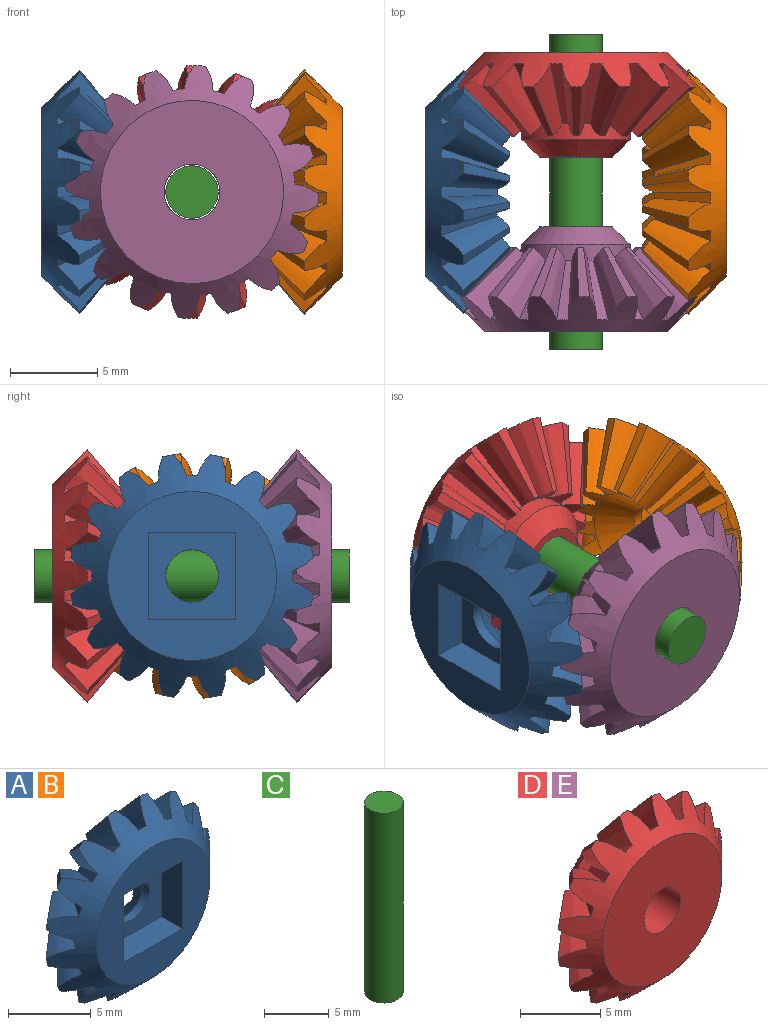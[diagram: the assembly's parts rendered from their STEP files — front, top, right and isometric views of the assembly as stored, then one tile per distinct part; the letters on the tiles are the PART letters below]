
ASSEMBLY  parts=5 mates=2
PART A: 74 faces, bbox 14.1x4.8x14.1 mm
  f0: bspline ~3.9x3.32mm, area 6.1mm2, adj f1,f16,f66,f71
  f1: cone r=6.97mm half-angle=45.1deg, axis (0,1,0), area 76.4mm2, adj f0,f2,f3,f4,f5,f6,f7,f8
  f2: bspline ~3.9x3.81mm, area 6.1mm2, adj f1,f24,f64,f66
  f3: bspline ~3.9x3.32mm, area 6.1mm2, adj f1,f58,f66,f73
  f4: bspline ~3.91x3.19mm, area 6.1mm2, adj f1,f59,f62,f66
  f5: bspline ~3.91x3.19mm, area 6.1mm2, adj f1,f19,f66,f73
  f6: plane 3.2x2.55mm, normal (0.72,0.62,-0.3), area 2mm2, adj f1,f12,f66,f69
  f7: cone r=3.9mm half-angle=50deg, axis (0,-1,0), area 2mm2, adj f1,f29,f37,f66
  f8: cone r=3.9mm half-angle=50deg, axis (0,-1,0), area 2mm2, adj f1,f28,f61,f66
  f9: bspline ~3.9x3.18mm, area 6.1mm2, adj f1,f32,f66,f72
  f10: bspline ~3.91x3.82mm, area 6.1mm2, adj f1,f15,f64,f66
  f11: bspline ~3.91x3.82mm, area 6.1mm2, adj f1,f33,f40,f66
  f12: bspline ~3.91x3.19mm, area 6.1mm2, adj f1,f6,f36,f66
  f13: bspline ~3.9x3.81mm, area 6.1mm2, adj f1,f23,f33,f66
  f14: bspline ~3.91x3.33mm, area 6.1mm2, adj f1,f66,f71,f72
  f15: cone r=3.9mm half-angle=50deg, axis (0,-1,0), area 2mm2, adj f1,f10,f26,f66
  f16: cone r=3.9mm half-angle=50deg, axis (0,-1,0), area 2mm2, adj f0,f1,f22,f66
  f17: plane 9.67x9.67mm, normal (0,-1,0), area 48.4mm2, adj f1,f45,f46,f48,f49
  f18: cylinder r=1.5mm len=3mm, axis (0,1,0), area 5.7mm2, adj f47,f50
  f19: plane 3.2x2.55mm, normal (-0.3,0.62,-0.72), area 2mm2, adj f1,f5,f60,f66
  f20: plane 3.2x2.16mm, normal (0.55,0.62,-0.55), area 2mm2, adj f1,f34,f51,f66
  f21: bspline ~3.91x3.87mm, area 6.1mm2, adj f1,f24,f30,f66
  f22: bspline ~3.91x3.19mm, area 6.1mm2, adj f1,f16,f39,f66
  f23: cone r=3.9mm half-angle=50deg, axis (0,-1,0), area 2mm2, adj f1,f13,f66,f70
  f24: cone r=3.9mm half-angle=50deg, axis (0,-1,0), area 2mm2, adj f1,f2,f21,f66
  f25: bspline ~3.91x3.33mm, area 6.1mm2, adj f1,f55,f65,f66
  f26: bspline ~3.92x3.89mm, area 6.1mm2, adj f1,f15,f39,f66
  f27: plane 3.2x2.55mm, normal (-0.72,0.62,-0.3), area 2mm2, adj f1,f37,f63,f66
  f28: bspline ~3.92x3.89mm, area 6.1mm2, adj f1,f8,f59,f66
  f29: bspline ~3.9x3.81mm, area 6.1mm2, adj f1,f7,f44,f66
  f30: plane 3.2x2.55mm, normal (-0.3,0.62,0.72), area 2mm2, adj f1,f21,f42,f66
  f31: cone r=3.9mm half-angle=50deg, axis (0,-1,0), area 2mm2, adj f1,f34,f35,f66
  f32: plane 3.2x2.55mm, normal (0.72,0.62,0.3), area 2mm2, adj f1,f9,f66,f70
  f33: plane 3.2x2.56mm, normal (0.78,0.62,0), area 2mm2, adj f1,f11,f13,f66
  f34: bspline ~3.91x3.33mm, area 6.1mm2, adj f1,f20,f31,f66
  f35: bspline ~3.9x3.18mm, area 6.1mm2, adj f1,f31,f52,f66
  f36: cone r=3.9mm half-angle=50deg, axis (0,-1,0), area 2mm2, adj f1,f12,f51,f66
  f37: bspline ~3.91x3.87mm, area 6.1mm2, adj f1,f7,f27,f66
  f38: bspline ~3.91x3.82mm, area 6.1mm2, adj f1,f43,f54,f66
  f39: plane 3.2x2.55mm, normal (0.3,0.62,0.72), area 2mm2, adj f1,f22,f26,f66
  f40: cone r=3.9mm half-angle=50deg, axis (0,-1,0), area 2mm2, adj f1,f11,f66,f69
  f41: bspline ~3.9x3.32mm, area 6.1mm2, adj f1,f55,f62,f66
  f42: bspline ~3.9x3.18mm, area 6.1mm2, adj f1,f30,f65,f66
  f43: plane 3.2x2.56mm, normal (0,0.62,-0.78), area 2mm2, adj f1,f38,f66,f67
  f44: plane 3.2x2.56mm, normal (-0.78,0.62,0), area 2mm2, adj f1,f29,f61,f66
  f45: plane 5x1.8mm, normal (0,0,-1), area 9mm2, adj f17,f46,f47,f49
  f46: plane 5x1.8mm, normal (1,0,0), area 9mm2, adj f17,f45,f47,f48
  f47: plane 5x5mm, normal (0,-1,0), area 17.9mm2, adj f18,f45,f46,f48,f49
  f48: plane 5x1.8mm, normal (0,0,1), area 9mm2, adj f17,f46,f47,f49
  f49: plane 5x1.8mm, normal (-1,0,0), area 9mm2, adj f17,f45,f47,f48
  f50: cone r=1.5mm half-angle=45deg, axis (0,1,0), area 32.7mm2, adj f18,f66
  f51: bspline ~3.9x3.32mm, area 6.1mm2, adj f1,f20,f36,f66
  f52: plane 3.2x2.55mm, normal (0.3,0.62,-0.72), area 2mm2, adj f1,f35,f53,f66
  f53: bspline ~3.91x3.87mm, area 6.1mm2, adj f1,f52,f66,f68
  f54: cone r=3.9mm half-angle=50deg, axis (0,-1,0), area 2mm2, adj f1,f38,f60,f66
  f55: plane 3.2x2.16mm, normal (-0.55,0.62,0.55), area 2mm2, adj f1,f25,f41,f66
  f56: cone r=3.9mm half-angle=50deg, axis (0,-1,0), area 2mm2, adj f1,f57,f63,f66
  f57: bspline ~3.91x3.33mm, area 6.1mm2, adj f1,f56,f58,f66
  f58: plane 3.2x2.16mm, normal (-0.55,0.62,-0.55), area 2mm2, adj f1,f3,f57,f66
  f59: plane 3.2x2.55mm, normal (-0.72,0.62,0.3), area 2mm2, adj f1,f4,f28,f66
  f60: bspline ~3.92x3.89mm, area 6.1mm2, adj f1,f19,f54,f66
  f61: bspline ~3.91x3.82mm, area 6.1mm2, adj f1,f8,f44,f66
  f62: cone r=3.9mm half-angle=50deg, axis (0,-1,0), area 2mm2, adj f1,f4,f41,f66
  f63: bspline ~3.9x3.18mm, area 6.1mm2, adj f1,f27,f56,f66
  f64: plane 3.2x2.56mm, normal (0,0.62,0.78), area 2mm2, adj f1,f2,f10,f66
  f65: cone r=3.9mm half-angle=50deg, axis (0,-1,0), area 2mm2, adj f1,f25,f42,f66
  f66: cone r=3.9mm half-angle=45.1deg, axis (0,1,0), area 13mm2, adj f0,f2,f3,f4,f5,f6,f7,f8
  f67: bspline ~3.9x3.81mm, area 6.1mm2, adj f1,f43,f66,f68
  f68: cone r=3.9mm half-angle=50deg, axis (0,-1,0), area 2mm2, adj f1,f53,f66,f67
  f69: bspline ~3.92x3.89mm, area 6.1mm2, adj f1,f6,f40,f66
  f70: bspline ~3.91x3.87mm, area 6.1mm2, adj f1,f23,f32,f66
  f71: plane 3.2x2.16mm, normal (0.55,0.62,0.55), area 2mm2, adj f0,f1,f14,f66
  f72: cone r=3.9mm half-angle=50deg, axis (0,-1,0), area 2mm2, adj f1,f9,f14,f66
  f73: cone r=3.9mm half-angle=50deg, axis (0,-1,0), area 2mm2, adj f1,f3,f5,f66
PART B: same geometry as A
PART C: 3 faces, bbox 3x3x18 mm
  f0: plane 3x3mm, normal (0,0,-1), area 7.1mm2, adj f2
  f1: plane 3x3mm, normal (0,0,1), area 7.1mm2, adj f2
  f2: cylinder r=1.5mm len=18mm, axis (0,0,-1), area 169.6mm2, adj f0,f1
PART D: 71 faces, bbox 14.5x6x14.5 mm
  f0: bspline ~4.12x4.03mm, area 6.6mm2, adj f2,f7,f27,f46
  f1: bspline ~4.13x4.09mm, area 6.6mm2, adj f2,f27,f46,f51
  f2: cone r=3.9mm half-angle=45.1deg, axis (0,1,0), area 13mm2, adj f0,f1,f3,f4,f5,f6,f7,f8
  f3: bspline ~4.12x3.5mm, area 6.6mm2, adj f2,f4,f28,f46
  f4: plane 3.43x2.29mm, normal (-0.55,0.62,-0.55), area 2.2mm2, adj f2,f3,f29,f46
  f5: bspline ~4.13x3.38mm, area 6.6mm2, adj f2,f46,f62,f70
  f6: plane 3.43x2.29mm, normal (-0.55,0.62,0.55), area 2.2mm2, adj f2,f46,f61,f63
  f7: plane 3.42x2.73mm, normal (0,0.62,-0.78), area 2.2mm2, adj f0,f2,f8,f46
  f8: bspline ~4.12x4.03mm, area 6.6mm2, adj f2,f7,f37,f46
  f9: bspline ~4.12x4.03mm, area 6.6mm2, adj f2,f33,f46,f67
  f10: bspline ~4.13x4.09mm, area 6.6mm2, adj f2,f33,f36,f46
  f11: bspline ~4.13x3.38mm, area 6.6mm2, adj f2,f12,f46,f65
  f12: plane 3.43x2.72mm, normal (-0.3,0.62,0.72), area 2.2mm2, adj f2,f11,f46,f69
  f13: bspline ~4.13x3.38mm, area 6.6mm2, adj f2,f14,f38,f46
  f14: plane 3.43x2.72mm, normal (0.3,0.62,-0.72), area 2.2mm2, adj f2,f13,f45,f46
  f15: cone r=3.9mm half-angle=50deg, axis (0,-1,0), area 2.2mm2, adj f2,f21,f39,f46
  f16: bspline ~4.12x4.03mm, area 6.6mm2, adj f2,f46,f59,f60
  f17: bspline ~4.13x4.09mm, area 6.6mm2, adj f2,f46,f59,f70
  f18: plane 3.43x2.72mm, normal (-0.72,0.62,-0.3), area 2.2mm2, adj f2,f46,f48,f50
  f19: plane 3.42x2.73mm, normal (0,0.62,0.78), area 2.2mm2, adj f2,f20,f46,f64
  f20: bspline ~4.12x4.03mm, area 6.6mm2, adj f2,f19,f32,f46
  f21: bspline ~4.13x4.09mm, area 6.6mm2, adj f2,f15,f35,f46
  f22: bspline ~4.13x3.38mm, area 6.6mm2, adj f2,f36,f42,f46
  f23: bspline ~4.13x3.51mm, area 6.6mm2, adj f2,f38,f41,f46
  f24: bspline ~4.13x3.51mm, area 6.6mm2, adj f2,f40,f46,f68
  f25: bspline ~4.12x3.5mm, area 6.6mm2, adj f2,f40,f44,f46
  f26: bspline ~4.13x3.38mm, area 6.6mm2, adj f2,f31,f44,f46
  f27: cone r=3.9mm half-angle=50deg, axis (0,-1,0), area 2.2mm2, adj f0,f1,f2,f46
  f28: cone r=3.9mm half-angle=50deg, axis (0,-1,0), area 2.2mm2, adj f2,f3,f46,f52
  f29: bspline ~4.13x3.51mm, area 6.6mm2, adj f2,f4,f46,f49
  f30: bspline ~4.13x4.09mm, area 6.6mm2, adj f2,f31,f32,f46
  f31: plane 3.43x2.72mm, normal (0.3,0.62,0.72), area 2.2mm2, adj f2,f26,f30,f46
  f32: cone r=3.9mm half-angle=50deg, axis (0,-1,0), area 2.2mm2, adj f2,f20,f30,f46
  f33: cone r=3.9mm half-angle=50deg, axis (0,-1,0), area 2.2mm2, adj f2,f9,f10,f46
  f34: bspline ~4.12x3.5mm, area 6.6mm2, adj f2,f41,f42,f46
  f35: plane 3.43x2.72mm, normal (0.72,0.62,0.3), area 2.2mm2, adj f2,f21,f43,f46
  f36: plane 3.43x2.72mm, normal (0.72,0.62,-0.3), area 2.2mm2, adj f2,f10,f22,f46
  f37: cone r=3.9mm half-angle=50deg, axis (0,-1,0), area 2.2mm2, adj f2,f8,f45,f46
  f38: cone r=3.9mm half-angle=50deg, axis (0,-1,0), area 2.2mm2, adj f2,f13,f23,f46
  f39: bspline ~4.12x4.03mm, area 6.6mm2, adj f2,f15,f46,f67
  f40: plane 3.43x2.29mm, normal (0.55,0.62,0.55), area 2.2mm2, adj f2,f24,f25,f46
  f41: plane 3.43x2.29mm, normal (0.55,0.62,-0.55), area 2.2mm2, adj f2,f23,f34,f46
  f42: cone r=3.9mm half-angle=50deg, axis (0,-1,0), area 2.2mm2, adj f2,f22,f34,f46
  f43: bspline ~4.13x3.38mm, area 6.6mm2, adj f2,f35,f46,f68
  f44: cone r=3.9mm half-angle=50deg, axis (0,-1,0), area 2.2mm2, adj f2,f25,f26,f46
  f45: bspline ~4.13x4.09mm, area 6.6mm2, adj f2,f14,f37,f46
  f46: cone r=6.97mm half-angle=45.1deg, axis (0,1,0), area 69.8mm2, adj f0,f1,f3,f4,f5,f6,f7,f8
  f47: bspline ~4.12x4.03mm, area 6.6mm2, adj f2,f46,f53,f60
  f48: bspline ~4.13x3.38mm, area 6.6mm2, adj f2,f18,f46,f49
  f49: cone r=3.9mm half-angle=50deg, axis (0,-1,0), area 2.2mm2, adj f2,f29,f46,f48
  f50: bspline ~4.13x4.09mm, area 6.6mm2, adj f2,f18,f46,f53
  f51: plane 3.43x2.72mm, normal (-0.3,0.62,-0.72), area 2.2mm2, adj f1,f2,f46,f52
  f52: bspline ~4.13x3.38mm, area 6.6mm2, adj f2,f28,f46,f51
  f53: cone r=3.9mm half-angle=50deg, axis (0,-1,0), area 2.2mm2, adj f2,f46,f47,f50
  f54: cylinder r=1.6mm len=6mm, axis (0,1,0), area 60.3mm2, adj f55,f57
  f55: plane 10.47x10.47mm, normal (0,-1,0), area 78mm2, adj f46,f54
  f56: cylinder r=3.1mm len=6.2mm, axis (0,-1,0), area 19.5mm2, adj f2,f58
  f57: plane 4.2x4.2mm, normal (0,1,0), area 5.8mm2, adj f54,f58
  f58: cone r=2.1mm half-angle=45deg, axis (0,-1,0), area 23.1mm2, adj f56,f57
  f59: cone r=3.9mm half-angle=50deg, axis (0,-1,0), area 2.2mm2, adj f2,f16,f17,f46
  f60: plane 3.43x2.74mm, normal (-0.78,0.62,0), area 2.2mm2, adj f2,f16,f46,f47
  f61: bspline ~4.12x3.5mm, area 6.6mm2, adj f2,f6,f46,f62
  f62: cone r=3.9mm half-angle=50deg, axis (0,-1,0), area 2.2mm2, adj f2,f5,f46,f61
  f63: bspline ~4.13x3.51mm, area 6.6mm2, adj f2,f6,f46,f65
  f64: bspline ~4.12x4.03mm, area 6.6mm2, adj f2,f19,f46,f66
  f65: cone r=3.9mm half-angle=50deg, axis (0,-1,0), area 2.2mm2, adj f2,f11,f46,f63
  f66: cone r=3.9mm half-angle=50deg, axis (0,-1,0), area 2.2mm2, adj f2,f46,f64,f69
  f67: plane 3.43x2.74mm, normal (0.78,0.62,0), area 2.2mm2, adj f2,f9,f39,f46
  f68: cone r=3.9mm half-angle=50deg, axis (0,-1,0), area 2.2mm2, adj f2,f24,f43,f46
  f69: bspline ~4.13x4.09mm, area 6.6mm2, adj f2,f12,f46,f66
  f70: plane 3.43x2.72mm, normal (-0.72,0.62,0.3), area 2.2mm2, adj f2,f5,f17,f46
PART E: same geometry as D
PLACE A rot(axis=(-0.71,-0.71,0),180deg) t=(8.08,8,8)mm
PLACE B rot(axis=(0.7,-0.7,0.12),166.5deg) t=(9.12,8,8)mm
PLACE C rot(axis=(0.63,0.55,-0.55),115.7deg) t=(8.6,8,8)mm fixed
PLACE D rot(axis=(0.77,0,-0.64),180deg) t=(8.6,7.92,8)mm
PLACE E rot(axis=(0,-1,0),7.6deg) t=(8.6,8.08,8)mm
MATE revolute E.f15 <-> C.f2  axis (0,-1,0) through (8.6,0,8)mm
MATE revolute C.f2 <-> D.f15  axis (0,1,0) through (8.6,17,8)mm
